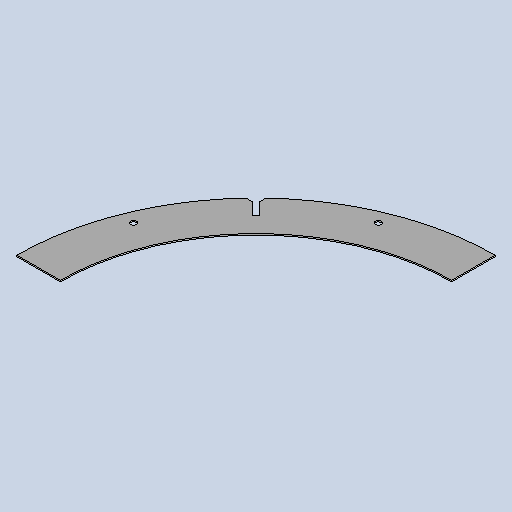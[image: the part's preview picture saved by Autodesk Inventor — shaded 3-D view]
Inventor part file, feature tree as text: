
AUTODESK INVENTOR PART (.ipt)
format: ipt  version: 2025 (Build 290162010, 162A)  size: 154,624 bytes
history: native  units: mm
features: other x4, sketch x3, sheet_metal_op x1, pattern_circular x1, extrude x1
ambient origin geometry x8: Origin, YZ Plane, XZ Plane, XY Plane, X Axis, Y Axis, Z Axis, Center Point
bodies: Solid1 (feature_tree)
feature tree (10):
  sheet_metal_op  "Face1"
  pattern_circular  "Circular Pattern1"  Count=110  [1 undecoded]
  extrude  "Extrusion1"  Depth=3.0mm
  other  "Corner Chamfer1"
  sketch  "Sketch1"  dims[d1=900.0mm d2=3.0mm]
  other  "Plate1"
  sketch  "Sketch2"  dims[d4=14.0mm]
  sketch  "Sketch3"  dims[d6=3.0mm d7=0.0mm d8=20.0mm d9=45.0deg d11=45.0deg d12=12.0mm d13=50.0mm d14=0.0mm d15=0.0mm d16=22.5deg d17=1040.0mm d18=10.0mm d19=6.0mm d20=45.0deg]
  other  "Cut1"
  other  "Definition1"
note: 1 required parameter value undecoded (feature->parameter linkage not recoverable at this tier; creation-order binding heuristic only, values carry confidence <= 0.55)
